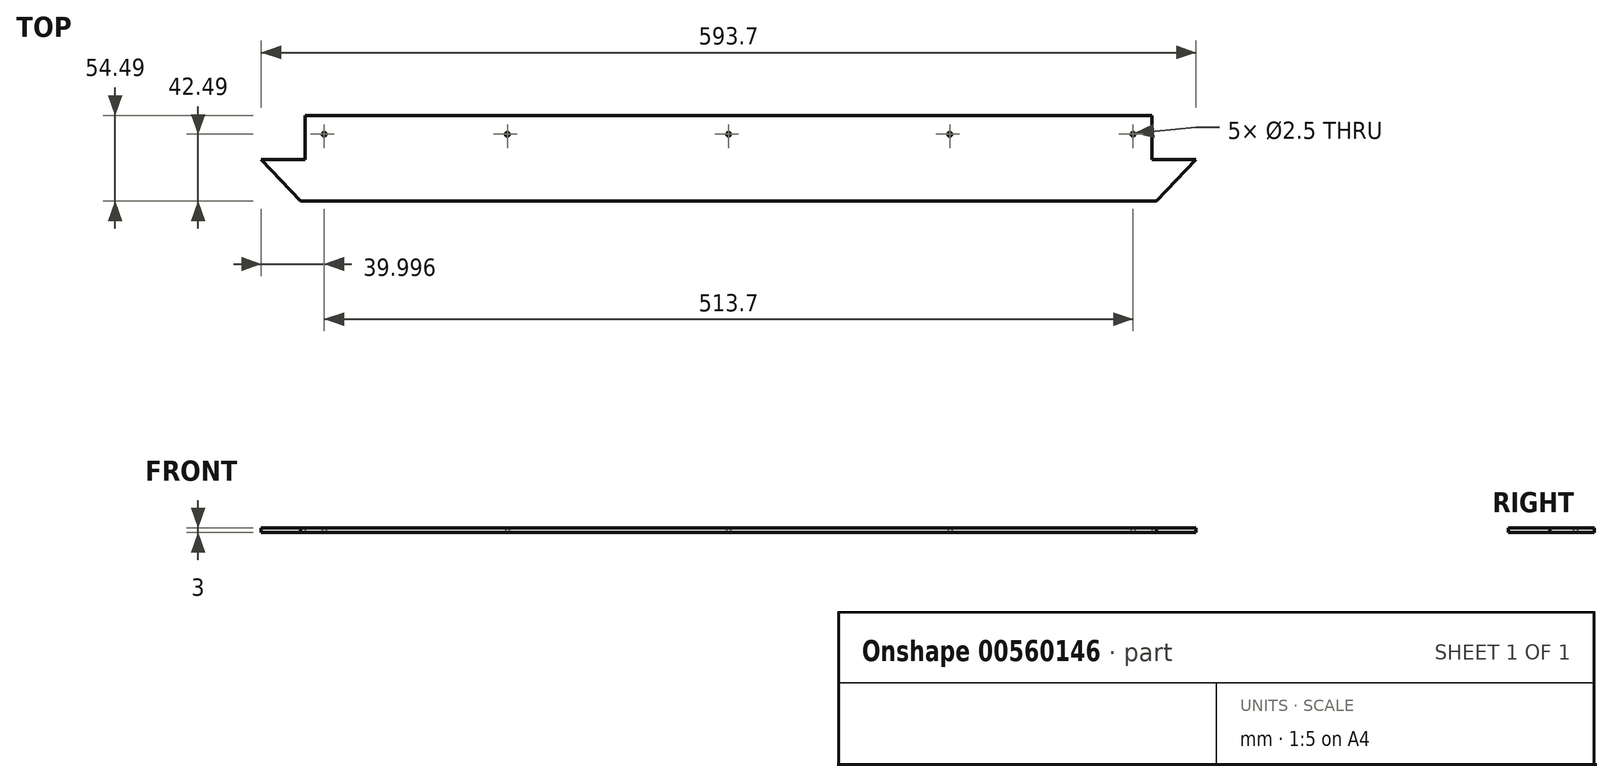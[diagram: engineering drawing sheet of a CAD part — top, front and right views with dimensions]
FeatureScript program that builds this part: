
annotation { "Feature Type Name" : "Feature", "Feature Type Description" : "" }
export const myFeature = defineFeature(function(context is Context, id is Id, definition is map)
    precondition{}
    {
        {
            var Q0;
            Q0=qCreatedBy(makeId("Top.planeOp"),FACE);
            var sketch = newSketch(context, id + "F0", { "sketchPlane" : qUnion([Q0])});
            skLineSegment(sketch, "E0", {"start": v(455.94, -26.49) * mm, "end": v(480.94, 0) * mm});
            skLineSegment(sketch, "E1", {"start": v(480.94, 0) * mm, "end": v(452.94, 0) * mm});
            skLineSegment(sketch, "E2", {"start": v(452.94, 0) * mm, "end": v(452.94, 28) * mm});
            skLineSegment(sketch, "E3", {"start": v(455.94, -26.49) * mm, "end": v(-87.76, -26.49) * mm});
            skLineSegment(sketch, "E4", {"start": v(-84.76, 28) * mm, "end": v(452.94, 28) * mm});
            skLineSegment(sketch, "E5", {"start": v(-87.76, -26.49) * mm, "end": v(-112.76, 0) * mm});
            skLineSegment(sketch, "E6", {"start": v(-112.76, 0) * mm, "end": v(-84.76, 0) * mm});
            skLineSegment(sketch, "E7", {"start": v(-84.76, 0) * mm, "end": v(-84.76, 28) * mm});
            skCircle(sketch, "E8", {"center": v(-72.76, 16) * mm, "radius": 1.25 * mm});
            skPoint(sketch, "E8.centerSnap0", {"position": v(-84.76, 14) * mm});
            skPoint(sketch, "E9.centerSnap0", {"position": v(184.09, 28) * mm});
            skPoint(sketch, "E10.centerSnap0", {"position": v(452.94, 14) * mm});
            skCircle(sketch, "E11", {"center": v(43.57, 16) * mm, "radius": 1.25 * mm});
            skCircle(sketch, "E12", {"center": v(184.09, 16) * mm, "radius": 1.25 * mm});
            skCircle(sketch, "E13", {"center": v(324.6, 16) * mm, "radius": 1.25 * mm});
            skCircle(sketch, "E14", {"center": v(440.94, 16) * mm, "radius": 1.25 * mm});
            skSolve(sketch);
        }
        {
            var Q0;
            Q0 = qSketchRegion(id + "F0", true);
            extrude(context, id + "F1", {"entities" : qUnion([Q0]), "depth" : 3 * mm, "offsetDistance" : 25 * mm});
        }
    });
